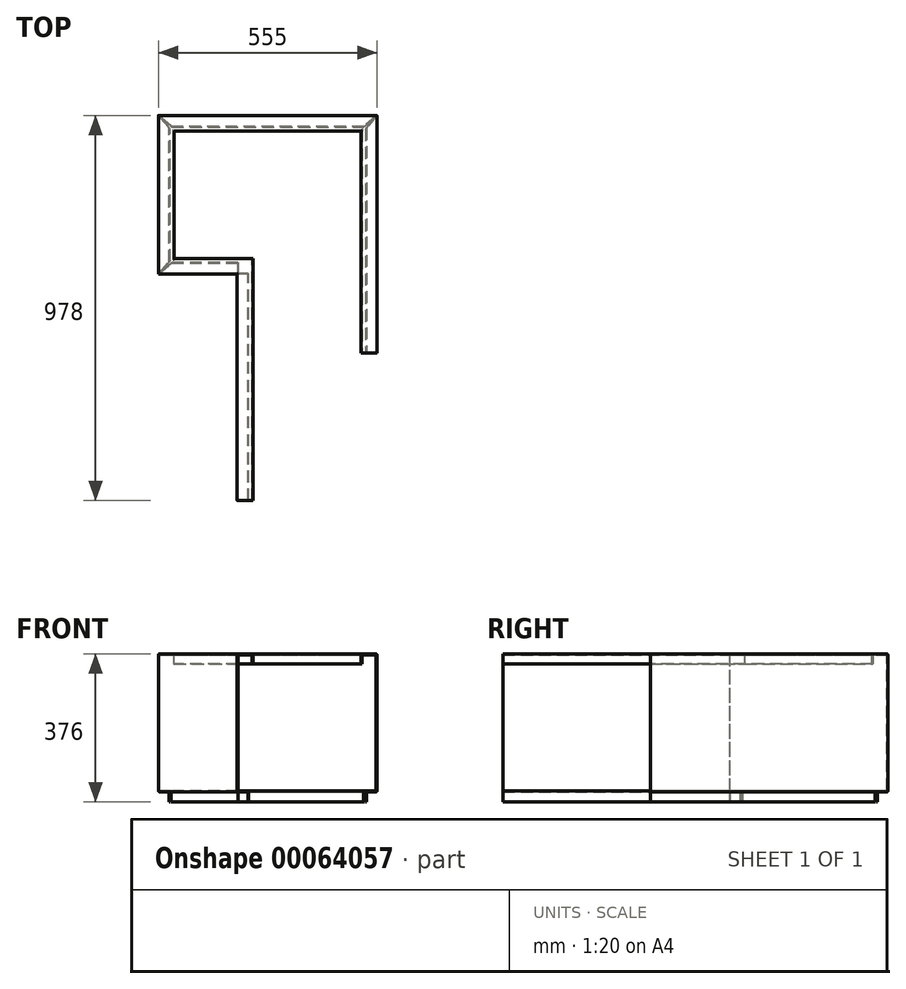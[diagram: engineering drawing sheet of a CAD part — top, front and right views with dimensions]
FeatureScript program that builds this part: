
annotation { "Feature Type Name" : "Feature", "Feature Type Description" : "" }
export const myFeature = defineFeature(function(context is Context, id is Id, definition is map)
    precondition{}
    {
        {
            var Q0;
            Q0=qCreatedBy(makeId("Front.planeOp"),FACE);
            var sketch = newSketch(context, id + "F0", { "sketchPlane" : qUnion([Q0])});
            skLineSegment(sketch, "E0", {"start": v(38, -25) * mm, "end": v(38, -4) * mm});
            skLineSegment(sketch, "E1", {"start": v(36, -2) * mm, "end": v(4, -2) * mm});
            skLineSegment(sketch, "E2", {"start": v(2, -4) * mm, "end": v(2, -346) * mm});
            skLineSegment(sketch, "E3", {"start": v(4, -348) * mm, "end": v(27, -348) * mm});
            skLineSegment(sketch, "E4", {"start": v(29, -350) * mm, "end": v(29, -376) * mm});
            skLineSegment(sketch, "E5.0", {"start": v(27, -352) * mm, "end": v(27, -376) * mm});
            skLineSegment(sketch, "E5.1", {"start": v(40, -25) * mm, "end": v(40, -2) * mm});
            skLineSegment(sketch, "E5.2", {"start": v(38, 0) * mm, "end": v(2, 0) * mm});
            skLineSegment(sketch, "E5.3", {"start": v(0, -2) * mm, "end": v(0, -348) * mm});
            skLineSegment(sketch, "E5.4", {"start": v(2, -350) * mm, "end": v(25, -350) * mm});
            skLineSegment(sketch, "E6", {"start": v(27, -376) * mm, "end": v(29, -376) * mm});
            skLineSegment(sketch, "E7", {"start": v(38, -25) * mm, "end": v(40, -25) * mm});
            skPoint(sketch, "E8.visualSharp", {"position": v(0, 0) * mm});
            skArc(sketch, "E8.filletArc", {"start": v(2, 0) * mm, "mid": v(0.59, -0.59) * mm, "end": v(0, -2) * mm});
            skArc(sketch, "E9.filletArc", {"start": v(4, -2) * mm, "mid": v(2.59, -2.59) * mm, "end": v(2, -4) * mm});
            skPoint(sketch, "E10.visualSharp", {"position": v(40, 0) * mm});
            skArc(sketch, "E10.filletArc", {"start": v(40, -2) * mm, "mid": v(39.41, -0.59) * mm, "end": v(38, 0) * mm});
            skArc(sketch, "E11.filletArc", {"start": v(38, -4) * mm, "mid": v(37.41, -2.59) * mm, "end": v(36, -2) * mm});
            skPoint(sketch, "E12.visualSharp", {"position": v(2, -348) * mm});
            skArc(sketch, "E12.filletArc", {"start": v(2, -346) * mm, "mid": v(2.59, -347.41) * mm, "end": v(4, -348) * mm});
            skPoint(sketch, "E13.visualSharp", {"position": v(0, -350) * mm});
            skArc(sketch, "E13.filletArc", {"start": v(0, -348) * mm, "mid": v(0.59, -349.41) * mm, "end": v(2, -350) * mm});
            skPoint(sketch, "E14.visualSharp", {"position": v(27, -350) * mm});
            skArc(sketch, "E14.filletArc", {"start": v(27, -352) * mm, "mid": v(26.41, -350.59) * mm, "end": v(25, -350) * mm});
            skPoint(sketch, "E15.visualSharp", {"position": v(29, -348) * mm});
            skArc(sketch, "E15.filletArc", {"start": v(29, -350) * mm, "mid": v(28.41, -348.59) * mm, "end": v(27, -348) * mm});
            skSolve(sketch);
        }
        {
            var Q0;
            Q0=qCreatedBy(makeId("Top.planeOp"),FACE);
            var sketch = newSketch(context, id + "F1", { "sketchPlane" : qUnion([Q0])});
            skLineSegment(sketch, "E16", {"start": v(0, 0) * mm, "end": v(0, 575) * mm});
            skLineSegment(sketch, "E17", {"start": v(0, 575) * mm, "end": v(-200, 575) * mm});
            skLineSegment(sketch, "E18", {"start": v(-200, 575) * mm, "end": v(-200, 978) * mm});
            skLineSegment(sketch, "E19", {"start": v(-200, 978) * mm, "end": v(355, 978) * mm});
            skLineSegment(sketch, "E20", {"start": v(355, 978) * mm, "end": v(355, 375) * mm});
            skSolve(sketch);
        }
        {
            var Q0;
            Q0=makeQuery(id+"F0.imprint","IMPRINT",FACE,{"disambiguationData":[TD([[makeQuery(id+"F0.imprint","IMPRINT",EDGE,{"derivedFrom":sQuery(id+"F0.wireOp",EDGE,"E0")}),-1.0]])]});
            var Q1;
            Q1=qConstructionFilter(qBodyType(qCreatedBy(id+"F1",EDGE),BodyType.WIRE),ConstructionObject.NO);
            sweep(context, id + "F2", {"profiles" : qUnion([Q0]), "path" : qUnion([Q1])});
        }
        {
            var Q0;
            Q0=makeQuery(id+"F2.opSweep","SWEPT_FACE",FACE,{"disambiguationData":[OSD([sQuery(id+"F0.wireOp",EDGE,"E3"),sQuery(id+"F1.wireOp",EDGE,"E16")])]});
            var sketch = newSketch(context, id + "F3", { "sketchPlane" : qUnion([Q0])});
            skLineSegment(sketch, "E21", {"start": v(2, 577) * mm, "end": v(2, 605.22) * mm});
            skLineSegment(sketch, "E22", {"start": v(2, 605.22) * mm, "end": v(30.14, 605.22) * mm});
            skLineSegment(sketch, "E23", {"start": v(30.14, 605.22) * mm, "end": v(30.14, 577) * mm});
            skLineSegment(sketch, "E24", {"start": v(30.14, 577) * mm, "end": v(2, 577) * mm});
            skLineSegment(sketch, "E25", {"start": v(-198, 577) * mm, "end": v(-171, 609.18) * mm});
            skLineSegment(sketch, "E26", {"start": v(-171, 609.18) * mm, "end": v(-169.38, 606) * mm});
            skLineSegment(sketch, "E27", {"start": v(-169.38, 606) * mm, "end": v(-165.82, 604) * mm});
            skLineSegment(sketch, "E28", {"start": v(-165.82, 604) * mm, "end": v(-198, 577) * mm});
            skLineSegment(sketch, "E29", {"start": v(-198, 976) * mm, "end": v(-171, 943.82) * mm});
            skLineSegment(sketch, "E30", {"start": v(-171, 943.82) * mm, "end": v(-167.14, 945) * mm});
            skLineSegment(sketch, "E31", {"start": v(-167.14, 945) * mm, "end": v(-165.82, 949) * mm});
            skLineSegment(sketch, "E32", {"start": v(-165.82, 949) * mm, "end": v(-198, 976) * mm});
            skLineSegment(sketch, "E33", {"start": v(353, 976) * mm, "end": v(320.37, 948.75) * mm});
            skLineSegment(sketch, "E34", {"start": v(320.37, 948.75) * mm, "end": v(325.78, 948.75) * mm});
            skLineSegment(sketch, "E35", {"start": v(325.78, 948.75) * mm, "end": v(325.86, 943.46) * mm});
            skLineSegment(sketch, "E36", {"start": v(325.86, 943.46) * mm, "end": v(353, 976) * mm});
            skSolve(sketch);
        }
        {
            var Q0;
            Q0=qSketchRegion(id+"F3",true);
            extrude(context, id + "F4", {"entities" : qUnion([Q0]), "operationType" : NewBodyOperationType.REMOVE, "oppositeDirection" : true, "depth" : 30 * mm});
        }
    });
